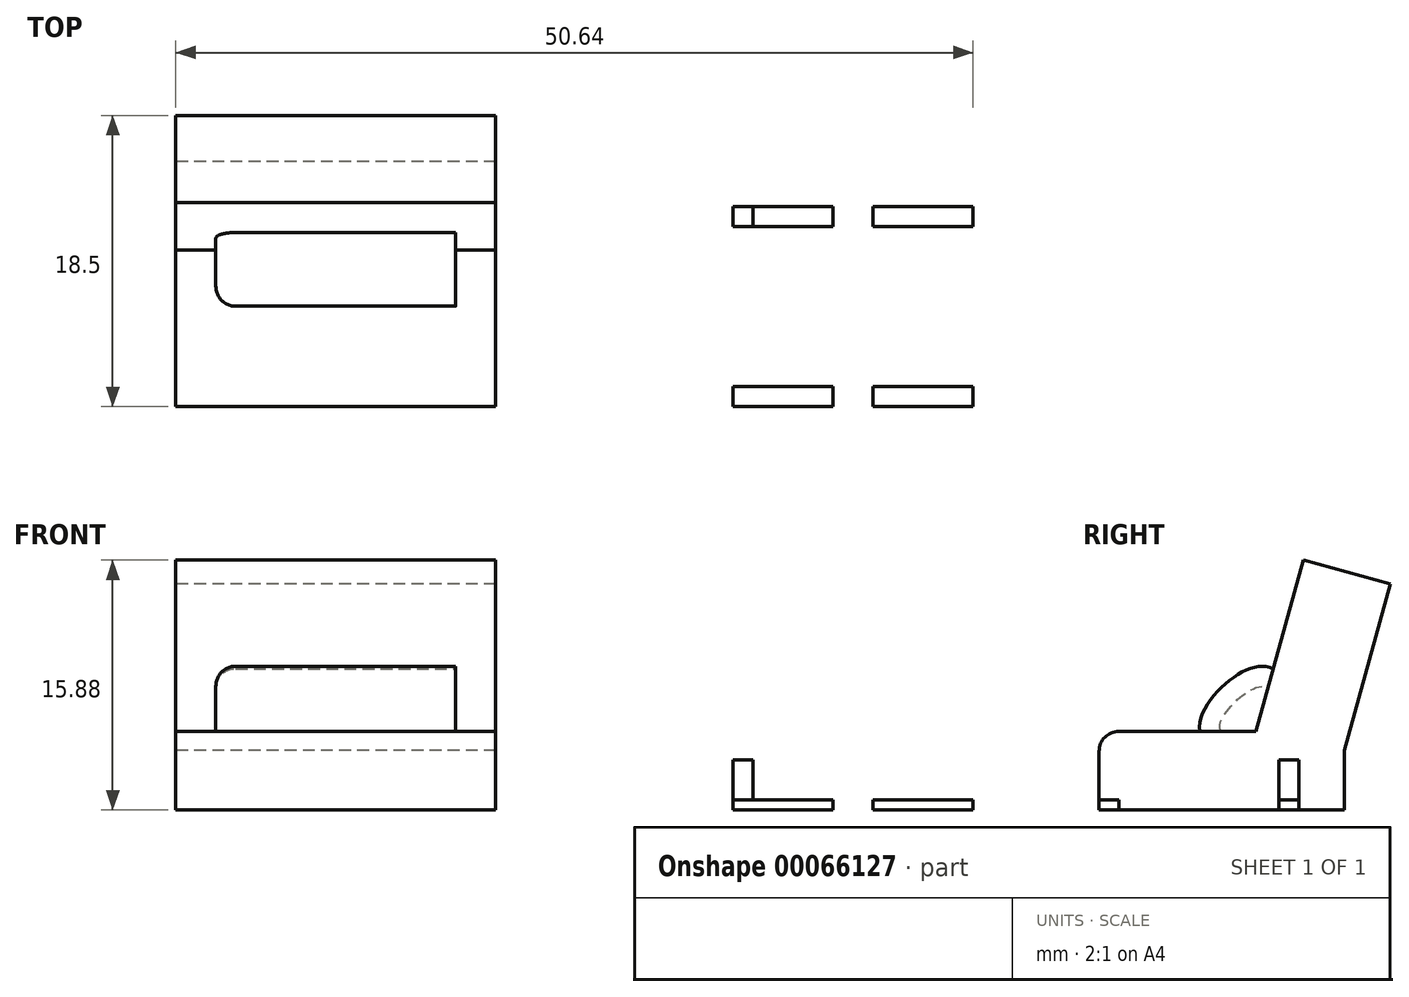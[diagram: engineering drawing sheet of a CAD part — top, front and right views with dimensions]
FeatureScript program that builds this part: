
annotation { "Feature Type Name" : "Feature", "Feature Type Description" : "" }
export const myFeature = defineFeature(function(context is Context, id is Id, definition is map)
    precondition{}
    {
        {
            var Q0;
            Q0=qCreatedBy(makeId("Right.planeOp"),FACE);
            var sketch = newSketch(context, id + "F0", { "sketchPlane" : qUnion([Q0])});
            skPoint(sketch, "E0.visualSharp", {"position": v(0, 18.95) * mm});
            skLineSegment(sketch, "E1", {"start": v(18.5, 14.35) * mm, "end": v(12.97, 15.88) * mm});
            skLineSegment(sketch, "E2", {"start": v(12.97, 15.88) * mm, "end": v(9.96, 5) * mm});
            skLineSegment(sketch, "E3", {"start": v(9.96, 5) * mm, "end": v(0, 5) * mm});
            skLineSegment(sketch, "E4", {"start": v(0, 5) * mm, "end": v(0, 0) * mm});
            skLineSegment(sketch, "E5", {"start": v(18.5, 14.35) * mm, "end": v(15.58, 3.8) * mm});
            skLineSegment(sketch, "E6", {"start": v(15.58, 3.8) * mm, "end": v(15.58, 0) * mm});
            skLineSegment(sketch, "E7", {"start": v(0, 0) * mm, "end": v(15.58, 0) * mm});
            skSolve(sketch);
        }
        {
            var Q0;
            Q0=makeQuery(id+"F0.imprint","IMPRINT",FACE,{"disambiguationData":[TD([[makeQuery(id+"F0.imprint","IMPRINT",EDGE,{"derivedFrom":sQuery(id+"F0.wireOp",EDGE,"E1")}),1.0]])]});
            extrude(context, id + "F1", {"entities" : qUnion([Q0]), "depth" : 20.32 * mm});
        }
        {
            var Q0;
            Q0=makeQuery(id+"F1.opExtrude","CAP_FACE",FACE,{"disambiguationData":[OSD([sQuery(id+"F0.wireOp",EDGE,"E1"),sQuery(id+"F0.wireOp",EDGE,"E2"),sQuery(id+"F0.wireOp",EDGE,"E3"),sQuery(id+"F0.wireOp",EDGE,"E4"),sQuery(id+"F0.wireOp",EDGE,"E5"),sQuery(id+"F0.wireOp",EDGE,"E6"),sQuery(id+"F0.wireOp",EDGE,"E7")])],"isStart":false});
            var sketch = newSketch(context, id + "F2", { "sketchPlane" : qUnion([Q0])});
            skFitSpline(sketch, "E8", {"points": [v(6.4, 5) * mm, v(8.43, 8.36) * mm, v(11.06, 8.98) * mm, v(12.15, 6.43) * mm, v(8.9, 3.25) * mm, v(6.4, 5) * mm]});
            skSolve(sketch);
        }
        {
            var Q0;
            {var subQ0=sQuery(id+"F2.wireOp",EDGE,"E8");var subQ1=makeQuery(id+"F1.opExtrude","CAP_EDGE",EDGE,{"disambiguationData":[OSD([sQuery(id+"F0.wireOp",EDGE,"E2")])],"isStart":false});var subQ2=makeQuery(id+"F2.imprint","INTERSECT",VERTEX,{"derivedFrom":[subQ1,subQ0]});Q0=makeQuery(id+"F2.imprint","IMPRINT",FACE,{"disambiguationData":[TD([[makeQuery(id+"F2.imprint","IMPRINT",EDGE,{"disambiguationData":[TD([[subQ2,1.0]])],"derivedFrom":subQ0}),-1.0]])]});}
            extrude(context, id + "F3", {"entities" : qUnion([Q0]), "operationType" : NewBodyOperationType.ADD, "oppositeDirection" : true, "depth" : 17.78 * mm});
        }
        {
            var Q0;
            {var subQ0=sQuery(id+"F0.wireOp",EDGE,"E3");var subQ1=sQuery(id+"F0.wireOp",EDGE,"E2");Q0=makeQuery(id+"F3.boolean.opBoolean","MERGE",FACE,{"derivedFrom":[makeQuery(id+"F1.opExtrude","CAP_FACE",FACE,{"disambiguationData":[OSD([sQuery(id+"F0.wireOp",EDGE,"E1"),subQ1,subQ0,sQuery(id+"F0.wireOp",EDGE,"E4"),sQuery(id+"F0.wireOp",EDGE,"E5"),sQuery(id+"F0.wireOp",EDGE,"E6"),sQuery(id+"F0.wireOp",EDGE,"E7")])],"isStart":false}),makeQuery(id+"F3.opExtrude","CAP_FACE",FACE,{"disambiguationData":[OSD([subQ1,subQ0,sQuery(id+"F2.wireOp",EDGE,"E8")])],"isStart":true})]});}
            var sketch = newSketch(context, id + "F4", { "sketchPlane" : qUnion([Q0])});
            skLineSegment(sketch, "E9", {"start": v(0, 5) * mm, "end": v(12.11, 5) * mm});
            skLineSegment(sketch, "E10", {"start": v(12.97, 15.88) * mm, "end": v(9.96, 5) * mm});
            skLineSegment(sketch, "E11", {"start": v(11.35, 10.05) * mm, "end": v(5.61, 10.59) * mm});
            skLineSegment(sketch, "E12", {"start": v(5.61, 10.59) * mm, "end": v(5.08, 5) * mm});
            skSolve(sketch);
        }
        {
            var Q0;
            {var subQ1=makeQuery(id+"F3.opExtrude","CAP_EDGE",EDGE,{"disambiguationData":[OSD([sQuery(id+"F2.wireOp",EDGE,"E8")])],"isStart":true});Q0=makeQuery(id+"F4.imprint","IMPRINT",FACE,{"disambiguationData":[TD([[makeQuery(id+"F4.imprint","IMPRINT",EDGE,{"derivedFrom":subQ1}),-1.0]])]});}
            extrude(context, id + "F5", {"entities" : qUnion([Q0]), "operationType" : NewBodyOperationType.REMOVE, "oppositeDirection" : true, "depth" : 2.54 * mm});
        }
        {
            var Q0;
            Q0=makeQuery(id+"F5.boolean.opBoolean","COPY",EDGE,{"derivedFrom":makeQuery(id+"F5.opExtrude","CAP_EDGE",EDGE,{"disambiguationData":[OSD([sQuery(id+"F2.wireOp",EDGE,"E8")])],"isStart":false})});
            var Q1;
            Q1=makeQuery(id+"F3.opExtrude","CAP_EDGE",EDGE,{"disambiguationData":[OSD([sQuery(id+"F2.wireOp",EDGE,"E8")])],"isStart":false});
            fillet(context, id + "F6", {"entities" : qUnion([Q0, Q1]), "radius" : 1.27 * mm, "tangentPropagation" : true, "allowEdgeOverflow" : false});
        }
        {
            var Q0;
            Q0=makeQuery(id+"F1.opExtrude","SWEPT_EDGE",EDGE,{"disambiguationData":[OSD([sQuery(id+"F0.wireOp",EDGE,"E3"),sQuery(id+"F0.wireOp",EDGE,"E4")])]});
            fillet(context, id + "F7", {"entities" : qUnion([Q0]), "radius" : 1.27 * mm, "tangentPropagation" : true, "allowEdgeOverflow" : false});
        }
        {
            var Q0;
            Q0=qCreatedBy(makeId("Top.planeOp"),FACE);
            var sketch = newSketch(context, id + "F8", { "sketchPlane" : qUnion([Q0])});
            skLineSegment(sketch, "E13.bottom", {"start": v(35.4, 12.7) * mm, "end": v(50.64, 12.7) * mm});
            skLineSegment(sketch, "E13.top", {"start": v(35.4, 0) * mm, "end": v(50.64, 0) * mm});
            skLineSegment(sketch, "E14", {"start": v(41.75, 12.7) * mm, "end": v(41.75, 0) * mm});
            skLineSegment(sketch, "E15", {"start": v(41.75, 0) * mm, "end": v(44.3, 0) * mm});
            skLineSegment(sketch, "E16", {"start": v(44.3, 0) * mm, "end": v(44.3, 12.7) * mm});
            skLineSegment(sketch, "E17", {"start": v(44.3, 12.7) * mm, "end": v(41.75, 12.7) * mm});
            skLineSegment(sketch, "E18.left", {"start": v(41.75, 12.7) * mm, "end": v(41.75, 11.43) * mm});
            skLineSegment(sketch, "E19.bottom", {"start": v(44.3, 12.7) * mm, "end": v(50.64, 12.7) * mm});
            skLineSegment(sketch, "E19.top", {"start": v(44.3, 11.43) * mm, "end": v(50.64, 11.43) * mm});
            skLineSegment(sketch, "E19.left", {"start": v(44.3, 12.7) * mm, "end": v(44.3, 11.43) * mm});
            skLineSegment(sketch, "E19.right", {"start": v(50.64, 12.7) * mm, "end": v(50.64, 11.43) * mm});
            skLineSegment(sketch, "E20", {"start": v(41.75, 11.43) * mm, "end": v(35.4, 11.43) * mm});
            skLineSegment(sketch, "E21", {"start": v(41.75, 1.27) * mm, "end": v(35.4, 1.27) * mm});
            skLineSegment(sketch, "E22", {"start": v(44.3, 1.27) * mm, "end": v(50.64, 1.27) * mm});
            skLineSegment(sketch, "E23", {"start": v(35.4, 12.7) * mm, "end": v(35.4, 11.43) * mm});
            skLineSegment(sketch, "E24", {"start": v(35.4, 1.27) * mm, "end": v(35.4, 0) * mm});
            skLineSegment(sketch, "E25", {"start": v(50.64, 1.27) * mm, "end": v(50.64, 0) * mm});
            skSolve(sketch);
        }
        {
            var Q0;
            Q0=makeQuery(id+"F8.imprint","IMPRINT",FACE,{"disambiguationData":[TD([[makeQuery(id+"F8.imprint","IMPRINT",EDGE,{"derivedFrom":sQuery(id+"F8.wireOp",EDGE,"E13.bottom")}),-1.0]])]});
            var Q1;
            {var subQ0=sQuery(id+"F8.wireOp",EDGE,"E15");Q1=makeQuery(id+"F8.imprint","IMPRINT",FACE,{"disambiguationData":[TD([[makeQuery(id+"F8.imprint","IMPRINT",EDGE,{"derivedFrom":subQ0}),1.0]])]});}
            var Q2;
            Q2=makeQuery(id+"F8.imprint","IMPRINT",FACE,{"disambiguationData":[TD([[makeQuery(id+"F8.imprint","IMPRINT",EDGE,{"derivedFrom":sQuery(id+"F8.wireOp",EDGE,"E19.bottom")}),-1.0]])]});
            var Q3;
            {var subQ4=sQuery(id+"F8.wireOp",EDGE,"E22");Q3=makeQuery(id+"F8.imprint","IMPRINT",FACE,{"disambiguationData":[TD([[makeQuery(id+"F8.imprint","IMPRINT",EDGE,{"derivedFrom":subQ4}),-1.0]])]});}
            var Q4;
            {var subQ4=sQuery(id+"F8.wireOp",EDGE,"E21");Q4=makeQuery(id+"F8.imprint","IMPRINT",FACE,{"disambiguationData":[TD([[makeQuery(id+"F8.imprint","IMPRINT",EDGE,{"derivedFrom":subQ4}),1.0]])]});}
            extrude(context, id + "F9", {"entities" : qUnion([Q0, Q1, Q2, Q3, Q4]), "depth" : 0.64 * mm});
        }
        {
            var Q0;
            Q0=makeQuery(id+"F9.opExtrude","CAP_FACE",FACE,{"disambiguationData":[OSD([sQuery(id+"F8.wireOp",EDGE,"E13.bottom"),sQuery(id+"F8.wireOp",EDGE,"E13.top"),sQuery(id+"F8.wireOp",EDGE,"E14"),sQuery(id+"F8.wireOp",EDGE,"E15"),sQuery(id+"F8.wireOp",EDGE,"E16"),sQuery(id+"F8.wireOp",EDGE,"E17"),sQuery(id+"F8.wireOp",EDGE,"E19.bottom"),sQuery(id+"F8.wireOp",EDGE,"E19.top"),sQuery(id+"F8.wireOp",EDGE,"E19.right"),sQuery(id+"F8.wireOp",EDGE,"E20"),sQuery(id+"F8.wireOp",EDGE,"E21"),sQuery(id+"F8.wireOp",EDGE,"E22"),sQuery(id+"F8.wireOp",EDGE,"E23"),sQuery(id+"F8.wireOp",EDGE,"E24"),sQuery(id+"F8.wireOp",EDGE,"E25")])],"isStart":false});
            var sketch = newSketch(context, id + "F10", { "sketchPlane" : qUnion([Q0])});
            skLineSegment(sketch, "E26.bottom", {"start": v(35.4, 12.7) * mm, "end": v(36.67, 12.7) * mm});
            skLineSegment(sketch, "E26.top", {"start": v(35.4, 11.43) * mm, "end": v(36.67, 11.43) * mm});
            skLineSegment(sketch, "E26.left", {"start": v(35.4, 12.7) * mm, "end": v(35.4, 11.43) * mm});
            skLineSegment(sketch, "E26.right", {"start": v(36.67, 12.7) * mm, "end": v(36.67, 11.43) * mm});
            skLineSegment(sketch, "E27.bottom", {"start": v(50.64, 12.7) * mm, "end": v(49.37, 12.7) * mm});
            skLineSegment(sketch, "E27.top", {"start": v(50.64, 11.43) * mm, "end": v(49.37, 11.43) * mm});
            skLineSegment(sketch, "E27.left", {"start": v(50.64, 12.7) * mm, "end": v(50.64, 11.43) * mm});
            skLineSegment(sketch, "E27.right", {"start": v(49.37, 12.7) * mm, "end": v(49.37, 11.43) * mm});
            skLineSegment(sketch, "E28.bottom", {"start": v(50.64, 1.27) * mm, "end": v(49.37, 1.27) * mm});
            skLineSegment(sketch, "E28.top", {"start": v(50.64, 0) * mm, "end": v(49.37, 0) * mm});
            skLineSegment(sketch, "E28.left", {"start": v(50.64, 1.27) * mm, "end": v(50.64, 0) * mm});
            skLineSegment(sketch, "E28.right", {"start": v(49.37, 1.27) * mm, "end": v(49.37, 0) * mm});
            skLineSegment(sketch, "E29.bottom", {"start": v(35.4, 1.27) * mm, "end": v(36.67, 1.27) * mm});
            skLineSegment(sketch, "E29.top", {"start": v(35.4, 0) * mm, "end": v(36.67, 0) * mm});
            skLineSegment(sketch, "E29.left", {"start": v(35.4, 1.27) * mm, "end": v(35.4, 0) * mm});
            skLineSegment(sketch, "E29.right", {"start": v(36.67, 1.27) * mm, "end": v(36.67, 0) * mm});
            skSolve(sketch);
        }
        {
            var Q0;
            Q0=makeQuery(id+"F10.imprint","IMPRINT",FACE,{"disambiguationData":[TD([[makeQuery(id+"F10.imprint","IMPRINT",EDGE,{"derivedFrom":sQuery(id+"F10.wireOp",EDGE,"E26.bottom")}),-1.0]])]});
            var Q1;
            Q1=makeQuery(id+"F10.imprint","IMPRINT",FACE,{"disambiguationData":[TD([[makeQuery(id+"F10.imprint","IMPRINT",EDGE,{"derivedFrom":sQuery(id+"F10.wireOp",EDGE,"E27.bottom")}),-1.0]])]});
            var Q2;
            Q2=makeQuery(id+"F10.imprint","IMPRINT",FACE,{"disambiguationData":[TD([[makeQuery(id+"F10.imprint","IMPRINT",EDGE,{"derivedFrom":sQuery(id+"F10.wireOp",EDGE,"E28.bottom")}),-1.0]])]});
            var Q3;
            Q3=makeQuery(id+"F10.imprint","IMPRINT",FACE,{"disambiguationData":[TD([[makeQuery(id+"F10.imprint","IMPRINT",EDGE,{"derivedFrom":sQuery(id+"F10.wireOp",EDGE,"E29.bottom")}),1.0]])]});
            extrude(context, id + "F11", {"entities" : qUnion([Q0, Q1, Q2, Q3]), "operationType" : NewBodyOperationType.ADD, "depth" : 2.54 * mm});
        }
    });
